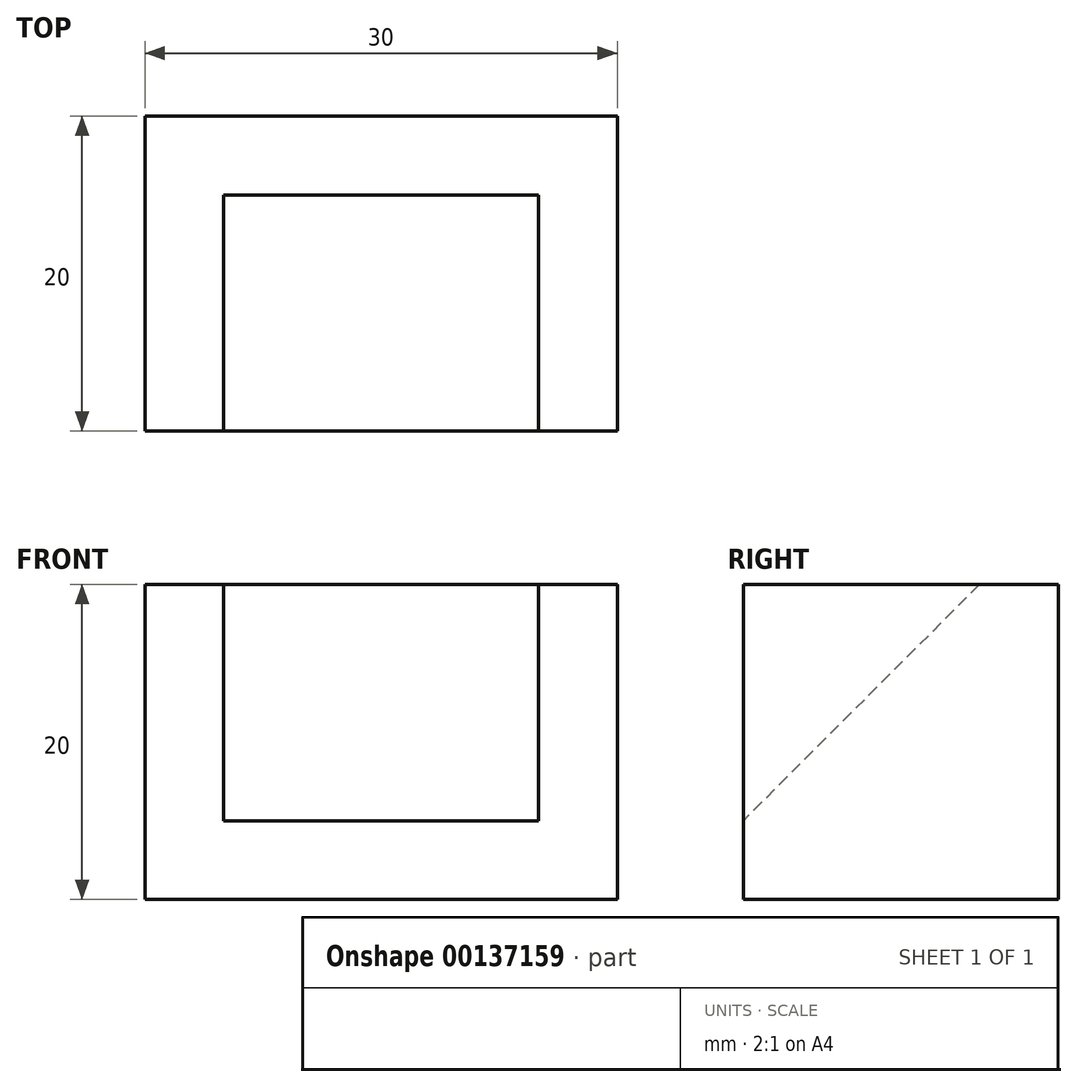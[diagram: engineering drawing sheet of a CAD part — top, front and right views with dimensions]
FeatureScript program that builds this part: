
annotation { "Feature Type Name" : "Feature", "Feature Type Description" : "" }
export const myFeature = defineFeature(function(context is Context, id is Id, definition is map)
    precondition{}
    {
        {
            var Q0;
            Q0=qCreatedBy(makeId("Top.planeOp"),FACE);
            var sketch = newSketch(context, id + "F0", { "sketchPlane" : qUnion([Q0])});
            skLineSegment(sketch, "E0.bottom", {"start": v(0, 0) * mm, "end": v(30, 0) * mm});
            skLineSegment(sketch, "E0.top", {"start": v(0, 20) * mm, "end": v(30, 20) * mm});
            skLineSegment(sketch, "E0.left", {"start": v(0, 0) * mm, "end": v(0, 20) * mm});
            skLineSegment(sketch, "E0.right", {"start": v(30, 0) * mm, "end": v(30, 20) * mm});
            skLineSegment(sketch, "E1", {"start": v(5, 0) * mm, "end": v(5, 20) * mm});
            skLineSegment(sketch, "E2", {"start": v(25, 20) * mm, "end": v(25, 0) * mm});
            skSolve(sketch);
        }
        {
            var Q0;
            {var subQ0=sQuery(id+"F0.wireOp",EDGE,"E0.left");Q0=makeQuery(id+"F0.imprint","IMPRINT",FACE,{"disambiguationData":[TD([[makeQuery(id+"F0.imprint","IMPRINT",EDGE,{"derivedFrom":subQ0}),-1.0]])]});}
            var Q1;
            {var subQ0=sQuery(id+"F0.wireOp",EDGE,"E0.right");Q1=makeQuery(id+"F0.imprint","IMPRINT",FACE,{"disambiguationData":[TD([[makeQuery(id+"F0.imprint","IMPRINT",EDGE,{"derivedFrom":subQ0}),1.0]])]});}
            var Q2;
            {var subQ0=sQuery(id+"F0.wireOp",EDGE,"E1");Q2=makeQuery(id+"F0.imprint","IMPRINT",FACE,{"disambiguationData":[TD([[makeQuery(id+"F0.imprint","IMPRINT",EDGE,{"derivedFrom":subQ0}),-1.0]])]});}
            extrude(context, id + "F1", {"entities" : qUnion([Q0, Q1, Q2]), "depth" : 20 * mm});
        }
        {
            var Q0;
            Q0=makeQuery(id+"F1.opExtrude","SWEPT_FACE",FACE,{"disambiguationData":[OSD([sQuery(id+"F0.wireOp",EDGE,"E0.right")])]});
            var sketch = newSketch(context, id + "F2", { "sketchPlane" : qUnion([Q0])});
            skLineSegment(sketch, "E3", {"start": v(0, 0) * mm, "end": v(0, 5) * mm, "construction": true});
            skLineSegment(sketch, "E4", {"start": v(20, 20) * mm, "end": v(15, 20) * mm, "construction": true});
            skLineSegment(sketch, "E5", {"start": v(15, 20) * mm, "end": v(0, 5) * mm});
            skSolve(sketch);
        }
        {
            var Q0;
            {var subQ0=sQuery(id+"F2.wireOp",EDGE,"E5");Q0=makeQuery(id+"F2.imprint","IMPRINT",FACE,{"disambiguationData":[TD([[makeQuery(id+"F2.imprint","IMPRINT",EDGE,{"derivedFrom":subQ0}),-1.0]])]});}
            extrude(context, id + "F3", {"entities" : qUnion([Q0]), "operationType" : NewBodyOperationType.REMOVE, "oppositeDirection" : true, "depth" : 25 * mm, "hasSecondDirection" : true, "secondDirectionOppositeDirection" : true, "secondDirectionDepth" : 5 * mm});
        }
    });
